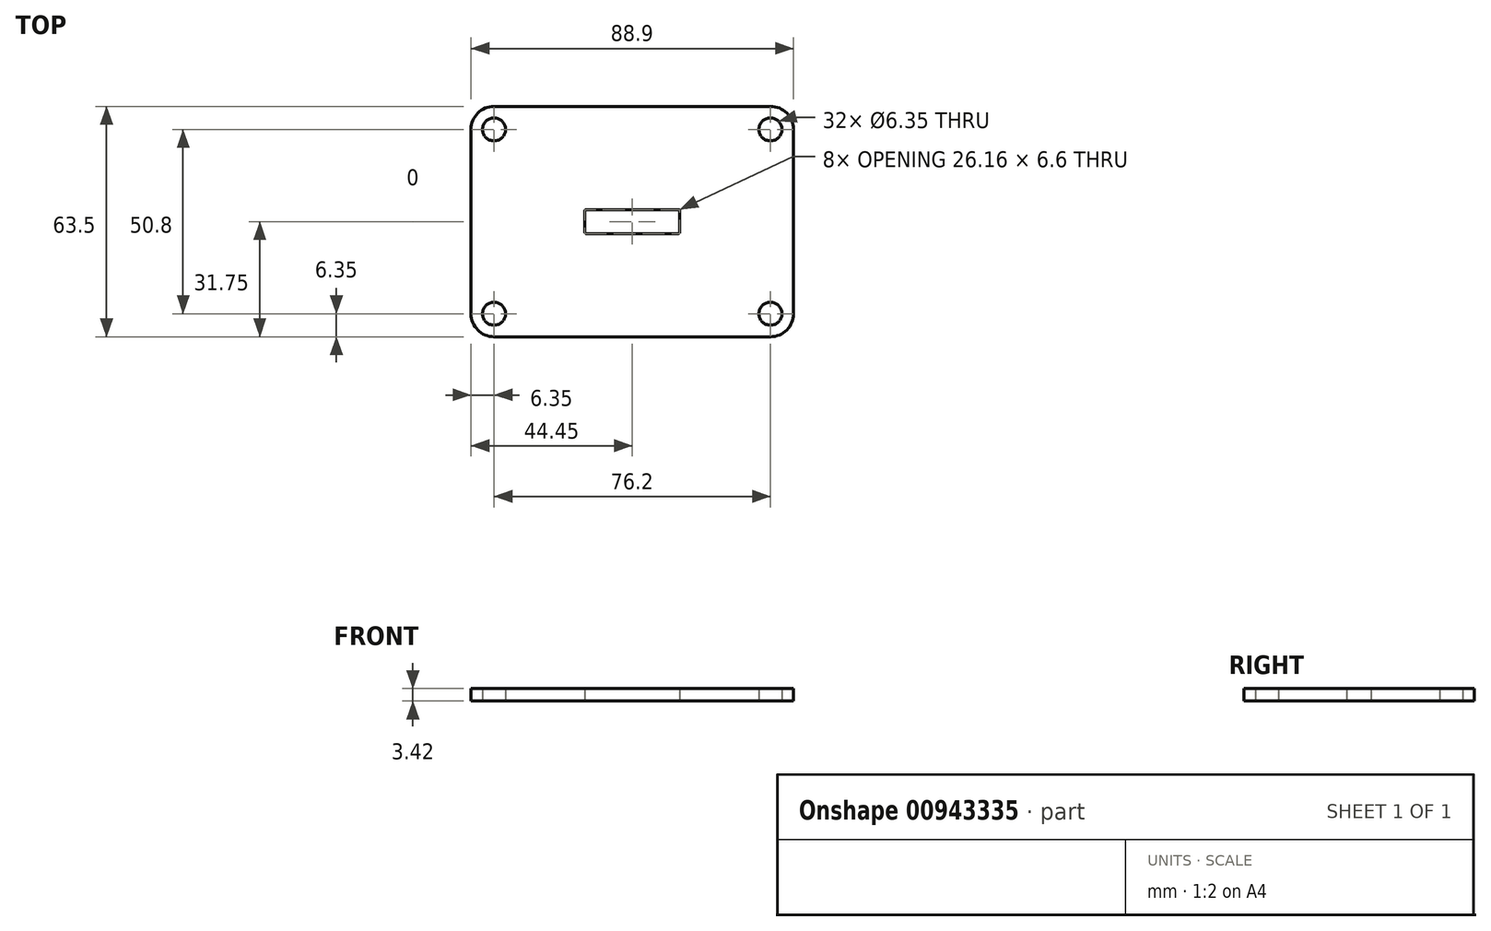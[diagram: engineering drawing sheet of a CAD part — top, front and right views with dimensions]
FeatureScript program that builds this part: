
annotation { "Feature Type Name" : "Feature", "Feature Type Description" : "" }
export const myFeature = defineFeature(function(context is Context, id is Id, definition is map)
    precondition{}
    {
        {
            var Q0;
            Q0=qCreatedBy(makeId("Top.planeOp"),FACE);
            var sketch = newSketch(context, id + "F0", { "sketchPlane" : qUnion([Q0])});
            skLineSegment(sketch, "E0.bottom", {"start": v(38.1, 31.75) * mm, "end": v(-38.1, 31.75) * mm});
            skLineSegment(sketch, "E0.top", {"start": v(38.1, -31.75) * mm, "end": v(-38.1, -31.75) * mm});
            skLineSegment(sketch, "E0.left", {"start": v(44.45, 25.4) * mm, "end": v(44.45, -25.4) * mm});
            skLineSegment(sketch, "E0.right", {"start": v(-44.45, 25.4) * mm, "end": v(-44.45, -25.4) * mm});
            skPoint(sketch, "E0.middle", {"position": v(0, 0) * mm});
            skLineSegment(sketch, "E1.bottom", {"start": v(12.76, 3.3) * mm, "end": v(-12.76, 3.3) * mm});
            skLineSegment(sketch, "E1.top", {"start": v(12.76, -3.3) * mm, "end": v(-12.76, -3.3) * mm});
            skLineSegment(sketch, "E1.left", {"start": v(13.08, 2.98) * mm, "end": v(13.08, -2.98) * mm});
            skLineSegment(sketch, "E1.right", {"start": v(-13.08, 2.98) * mm, "end": v(-13.08, -2.98) * mm});
            skPoint(sketch, "E2.visualSharp", {"position": v(-44.45, 31.75) * mm});
            skArc(sketch, "E2.filletArc", {"start": v(-38.1, 31.75) * mm, "mid": v(-42.6, 29.9) * mm, "end": v(-44.45, 25.4) * mm});
            skPoint(sketch, "E3.visualSharp", {"position": v(-44.45, -31.75) * mm});
            skArc(sketch, "E3.filletArc", {"start": v(-44.45, -25.4) * mm, "mid": v(-42.6, -29.9) * mm, "end": v(-38.1, -31.75) * mm});
            skPoint(sketch, "E4.visualSharp", {"position": v(44.45, -31.75) * mm});
            skArc(sketch, "E4.filletArc", {"start": v(38.1, -31.75) * mm, "mid": v(42.6, -29.9) * mm, "end": v(44.45, -25.4) * mm});
            skPoint(sketch, "E5.visualSharp", {"position": v(44.45, 31.75) * mm});
            skArc(sketch, "E5.filletArc", {"start": v(44.45, 25.4) * mm, "mid": v(42.6, 29.9) * mm, "end": v(38.1, 31.75) * mm});
            skPoint(sketch, "E6.visualSharp", {"position": v(-13.08, 3.3) * mm});
            skArc(sketch, "E6.filletArc", {"start": v(-12.76, 3.3) * mm, "mid": v(-12.99, 3.2) * mm, "end": v(-13.08, 2.98) * mm});
            skPoint(sketch, "E7.visualSharp", {"position": v(-13.08, -3.3) * mm});
            skArc(sketch, "E7.filletArc", {"start": v(-13.08, -2.98) * mm, "mid": v(-12.99, -3.2) * mm, "end": v(-12.76, -3.3) * mm});
            skPoint(sketch, "E8.visualSharp", {"position": v(13.08, -3.3) * mm});
            skArc(sketch, "E8.filletArc", {"start": v(12.76, -3.3) * mm, "mid": v(12.99, -3.2) * mm, "end": v(13.08, -2.98) * mm});
            skPoint(sketch, "E9.visualSharp", {"position": v(13.08, 3.3) * mm});
            skArc(sketch, "E9.filletArc", {"start": v(13.08, 2.98) * mm, "mid": v(12.99, 3.2) * mm, "end": v(12.76, 3.3) * mm});
            skCircle(sketch, "E10", {"center": v(-38.1, 25.4) * mm, "radius": 3.18 * mm});
            skCircle(sketch, "E11", {"center": v(-38.1, -25.4) * mm, "radius": 3.18 * mm});
            skCircle(sketch, "E12", {"center": v(38.1, -25.4) * mm, "radius": 3.18 * mm});
            skCircle(sketch, "E13", {"center": v(38.1, 25.4) * mm, "radius": 3.18 * mm});
            skSolve(sketch);
        }
        {
            var Q0;
            Q0=makeQuery(id+"F0.imprint","IMPRINT",FACE,{"disambiguationData":[TD([[makeQuery(id+"F0.imprint","IMPRINT",EDGE,{"derivedFrom":sQuery(id+"F0.wireOp",EDGE,"E0.bottom")}),1.0]])]});
            extrude(context, id + "F1", {"entities" : qUnion([Q0]), "endBound" : BoundingType.SYMMETRIC, "depth" : 3.42 * mm, "offsetDistance" : 25.4 * mm});
        }
    });
